# Revit family: Toilet-Floor_Mount-Sloan-WETS-4009_Series (Standard)
name_source: partatom
category: Plumbing Fixtures
revit_build: Autodesk Revit 2018 (Build: 20170223_1515(x64)
units: mm (PartAtom-declared; Revit-internal decimal feet)

## family parameters
Always vertical = No
Cut with Voids When Loaded = No
OmniClass Number = 23.45.05.21.11.11
OmniClass Title = Water Operated Water Closets
Part Type = Normal
Room Calculation Point = No
Round Connector Dimension = Use Radius
Shared = Yes
Work Plane-Based = Yes

## types (24) — shared parameters
ADA Compliant = No
Assembly Code = D2010110
CW Connection = Yes
CWFU = 3
Cold Water Connection Diameter = 1/2"
Cold Water Connection Radius = 1/4"
Default Elevation = 0"
Description = Standard floor mounted elongated pressure assist toilet
Fixture Color = White
HW Connection = No
Height = 29 3/4"
Manufacturer = Sloan
Material = Vitreous China-Sloan-White
Mounting = Floor Mount
Price = Prices may vary. Please consult Manufacturer Representative for most up-to-date price list.
Revision Date = 8/13/2021
URL = https://www.sloan.com
Vent Connection = No
WFU = 3
Waste Connection = Yes
Waste Connection Diameter = 2 1/8"
Waste Connection Radius = 1 1/16"
Width = 14 7/8"
zero-valued in all types: HWFU

## per-type parameters (varying)
| type | Flush Volume(s)/Flow Rate(s) | Left Handle | Left Handle With SloanTec | Length | Model | Right Handle | Right Handle With SloanTec | Rough-in | Toilet Geometry |
| WETS-4009.4213 | 1.6 gpf/6.8 Lpf | Yes | No | 27 1/2" | WETS-4009.4213 | No | No | 10" | WETS-4009-10-Inch Rough In : WETS-4009 10" Rough In |
| WETS-4009.4211 | 1.1 gpf/4.2 Lpf | Yes | No | 27 1/2" | WETS-4009.4211 | No | No | 10" | WETS-4009-10-Inch Rough In : WETS-4009 10" Rough In |
| WETS-4009.4210 | 1.28 gpf/4.8 Lpf | Yes | No | 27 1/2" | WETS-4009.4210 | No | No | 10" | WETS-4009-10-Inch Rough In : WETS-4009 10" Rough In |
| WETS-4009.4313 | 1.6 gpf/6.8 Lpf | No | No | 27 1/2" | WETS-4009.4313 | Yes | No | 10" | WETS-4009-10-Inch Rough In : WETS-4009 10" Rough In |
| WETS-4009.4311 | 1.1 gpf/4.2 Lpf | No | No | 27 1/2" | WETS-4009.4311 | Yes | No | 10" | WETS-4009-10-Inch Rough In : WETS-4009 10" Rough In |
| WETS-4009.4310 | 1.28 gpf/4.8 Lpf | No | No | 27 1/2" | WETS-4009.4310 | Yes | No | 10" | WETS-4009-10-Inch Rough In : WETS-4009 10" Rough In |
| WETS-4009.4013 | 1.6 gpf/6.8 Lpf | Yes | No | 29 1/2" | WETS-4009.4013 | No | No | 12" | WETS-4009-12-Inch Rough In : WETS-4009 12" Rough In |
| WETS-4009.4011 | 1.1 gpf/4.2 Lpf | Yes | No | 29 1/2" | WETS-4009.4011 | No | No | 12" | WETS-4009-12-Inch Rough In : WETS-4009 12" Rough In |
| WETS-4009.4010 | 1.28 gpf/4.8 Lpf | Yes | No | 29 1/2" | WETS-4009.4010 | No | No | 12" | WETS-4009-12-Inch Rough In : WETS-4009 12" Rough In |
| WETS-4009.4113 | 1.6 gpf/6.8 Lpf | No | No | 29 1/2" | WETS-4009.4113 | Yes | No | 12" | WETS-4009-12-Inch Rough In : WETS-4009 12" Rough In |
| WETS-4009.4111 | 1.1 gpf/4.2 Lpf | No | No | 29 1/2" | WETS-4009.4111 | Yes | No | 12" | WETS-4009-12-Inch Rough In : WETS-4009 12" Rough In |
| WETS-4009.4110 | 1.28 gpf/4.8 Lpf | No | No | 29 1/2" | WETS-4009.4110 | Yes | No | 12" | WETS-4009-12-Inch Rough In : WETS-4009 12" Rough In |
| WETS-4009.4011-STG | 1.1 gpf/4.2 Lpf | No | Yes | 29 1/2" | WETS-4009.4011-STG | No | No | 12" | WETS-4009-12-Inch Rough In : WETS-4009 12" Rough In |
| WETS-4009.4010-STG | 1.28 gpf/4.8 Lpf | No | Yes | 29 1/2" | WETS-4009.4010-STG | No | No | 12" | WETS-4009-12-Inch Rough In : WETS-4009 12" Rough In |
| WETS-4009.4013-STG | 1.6 gpf/6.8 Lpf | No | Yes | 29 1/2" | WETS-4009.4313-STG | No | No | 12" | WETS-4009-12-Inch Rough In : WETS-4009 12" Rough In |
| WETS-4009.4211-STG | 1.1 gpf/4.2 Lpf | No | Yes | 27 1/2" | WETS-4009.4211-STG | No | No | 10" | WETS-4009-10-Inch Rough In : WETS-4009 10" Rough In |
| WETS-4009.4210-STG | 1.28 gpf/4.8 Lpf | No | Yes | 27 1/2" | WETS-4009.4210-STG | No | No | 10" | WETS-4009-10-Inch Rough In : WETS-4009 10" Rough In |
| WETS-4009.4213-STG | 1.6 gpf/6.8 Lpf | No | Yes | 27 1/2" | WETS-4009.4213-STG | No | No | 10" | WETS-4009-10-Inch Rough In : WETS-4009 10" Rough In |
| WETS-4009.4111-STG | 1.1 gpf/4.2 Lpf | No | No | 29 1/2" | WETS-4009.4111-STG | No | Yes | 12" | WETS-4009-12-Inch Rough In : WETS-4009 12" Rough In |
| WETS-4009.4110-STG | 1.28 gpf/4.8 Lpf | No | No | 27 1/2" | WETS-4009.4110-STG | No | Yes | 12" | WETS-4009-12-Inch Rough In : WETS-4009 12" Rough In |
| WETS-4009.4113-STG | 1.6 gpf/6.8 Lpf | No | No | 29 1/2" | WETS-4009.4313-STG | No | Yes | 12" | WETS-4009-12-Inch Rough In : WETS-4009 12" Rough In |
| WETS-4009.4311-STG | 1.1 gpf/4.2 Lpf | No | No | 27 1/2" | WETS-4009.4311-STG | No | Yes | 10" | WETS-4009-10-Inch Rough In : WETS-4009 10" Rough In |
| WETS-4009.4310-STG | 1.28 gpf/4.8 Lpf | No | No | 27 1/2" | WETS-4009.4310-STG | No | Yes | 10" | WETS-4009-10-Inch Rough In : WETS-4009 10" Rough In |
| WETS-4009.4313-STG | 1.6 gpf/6.8 Lpf | No | No | 27 1/2" | WETS-4009.4313-STG | No | Yes | 10" | WETS-4009-10-Inch Rough In : WETS-4009 10" Rough In |

## geometry (parser evidence)
native form markers: Sweep x10
no freeform markers — native parametric forms only
